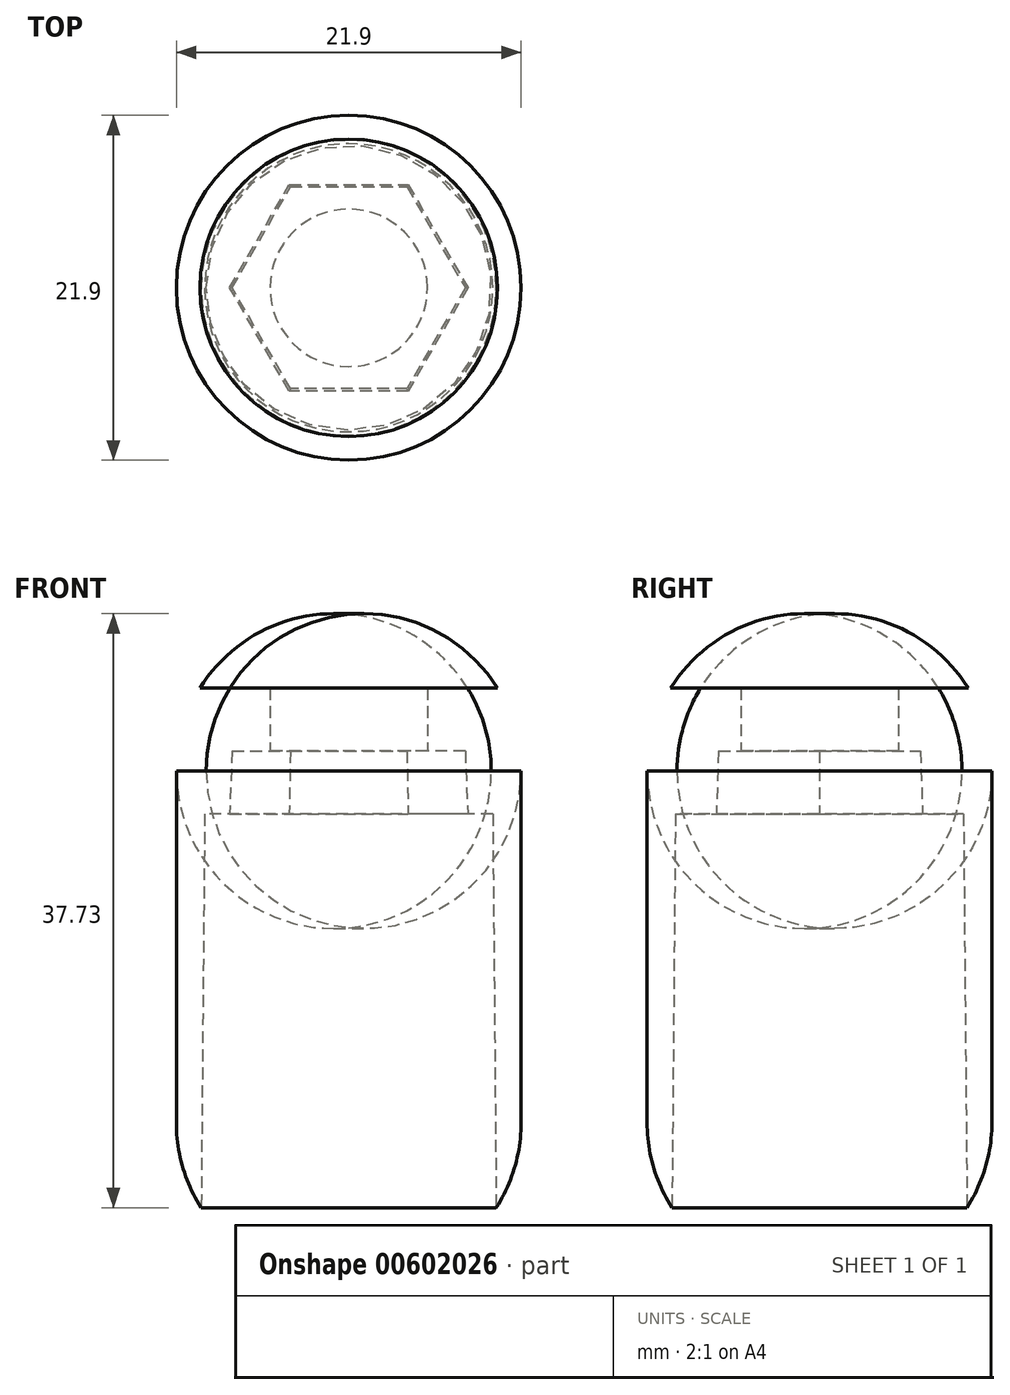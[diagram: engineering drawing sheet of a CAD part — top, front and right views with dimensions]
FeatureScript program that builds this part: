
annotation { "Feature Type Name" : "Feature", "Feature Type Description" : "" }
export const myFeature = defineFeature(function(context is Context, id is Id, definition is map)
    precondition{}
    {
        {
            var Q0;
            Q0=qCreatedBy(makeId("Top.planeOp"),FACE);
            var sketch = newSketch(context, id + "F0", { "sketchPlane" : qUnion([Q0])});
            skCircle(sketch, "E0", {"center": v(0, 0) * mm, "radius": 9.15 * mm});
            skCircle(sketch, "E1.cCircle", {"center": v(0, 0) * mm, "radius": 6.55 * mm, "construction": true});
            skLineSegment(sketch, "E1.0", {"start": v(-3.78, 6.55) * mm, "end": v(3.78, 6.55) * mm});
            skLineSegment(sketch, "E1.1", {"start": v(3.78, 6.55) * mm, "end": v(7.56, 0) * mm});
            skLineSegment(sketch, "E1.2", {"start": v(7.56, 0) * mm, "end": v(3.78, -6.55) * mm});
            skLineSegment(sketch, "E1.3", {"start": v(3.78, -6.55) * mm, "end": v(-3.78, -6.55) * mm});
            skLineSegment(sketch, "E1.4", {"start": v(-3.78, -6.55) * mm, "end": v(-7.56, 0) * mm});
            skLineSegment(sketch, "E1.5", {"start": v(-7.56, 0) * mm, "end": v(-3.78, 6.55) * mm});
            skPoint(sketch, "E1.0.midPoint", {"position": v(0, 6.55) * mm});
            skCircle(sketch, "E2.0", {"center": v(0, 0) * mm, "radius": 10.95 * mm});
            skSolve(sketch);
        }
        {
            var Q0;
            Q0=makeQuery(id+"F0.imprint","IMPRINT",FACE,{"disambiguationData":[TD([[makeQuery(id+"F0.imprint","IMPRINT",EDGE,{"derivedFrom":sQuery(id+"F0.wireOp",EDGE,"E0")}),-1.0]])]});
            extrude(context, id + "F1", {"entities" : qUnion([Q0]), "oppositeDirection" : true, "depth" : 25 * mm, "offsetDistance" : 25 * mm});
        }
        {
            var Q0;
            Q0=makeQuery(id+"F0.imprint","IMPRINT",FACE,{"disambiguationData":[TD([[makeQuery(id+"F0.imprint","IMPRINT",EDGE,{"derivedFrom":sQuery(id+"F0.wireOp",EDGE,"E0")}),1.0]])]});
            var Q1;
            Q1=makeQuery(id+"F0.imprint","IMPRINT",FACE,{"disambiguationData":[TD([[makeQuery(id+"F0.imprint","IMPRINT",EDGE,{"derivedFrom":sQuery(id+"F0.wireOp",EDGE,"E1.0")}),-1.0]])]});
            extrude(context, id + "F2", {"entities" : qUnion([Q0, Q1]), "operationType" : NewBodyOperationType.REMOVE, "oppositeDirection" : true, "depth" : 25 * mm, "offsetDistance" : 25 * mm, "hasDraft" : true, "draftAngle" : 0.5 * degree});
        }
        {
            var Q0;
            Q0=makeQuery(id+"F0.imprint","IMPRINT",FACE,{"disambiguationData":[TD([[makeQuery(id+"F0.imprint","IMPRINT",EDGE,{"derivedFrom":sQuery(id+"F0.wireOp",EDGE,"E1.0")}),-1.0]])]});
            var Q1;
            Q1=makeQuery(id+"F0.imprint","IMPRINT",FACE,{"disambiguationData":[TD([[makeQuery(id+"F0.imprint","IMPRINT",EDGE,{"derivedFrom":sQuery(id+"F0.wireOp",EDGE,"E0")}),1.0]])]});
            var Q2;
            Q2=makeQuery(id+"F0.imprint","IMPRINT",FACE,{"disambiguationData":[TD([[makeQuery(id+"F0.imprint","IMPRINT",EDGE,{"derivedFrom":sQuery(id+"F0.wireOp",EDGE,"E0")}),-1.0]])]});
            var Q3;
            Q3=sQuery(id+"F0.wireOp",EDGE,"E0");
            var Q4;
            Q4=sQuery(id+"F0.wireOp",EDGE,"E2.0");
            extrude(context, id + "F3", {"entities" : qUnion([Q0, Q1, Q2]), "operationType" : NewBodyOperationType.ADD, "surfaceEntities" : qUnion([Q3, Q4]), "depth" : 8 * mm, "offsetDistance" : 25 * mm});
        }
        {
            var Q0;
            Q0=makeQuery(id+"F0.imprint","IMPRINT",FACE,{"disambiguationData":[TD([[makeQuery(id+"F0.imprint","IMPRINT",EDGE,{"derivedFrom":sQuery(id+"F0.wireOp",EDGE,"E1.0")}),-1.0]])]});
            extrude(context, id + "F4", {"entities" : qUnion([Q0]), "operationType" : NewBodyOperationType.REMOVE, "depth" : 4 * mm, "offsetDistance" : 25 * mm, "hasDraft" : true, "draftAngle" : 2 * degree, "draftPullDirection" : true});
        }
        {
            var Q0;
            Q0=sQuery(id+"F0.wireOp",VERTEX,"E2.0.center");
            var Q1;
            Q1=makeQuery(id+"F1.opExtrude","SWEPT_BODY",BODY,{"disambiguationData":[OSD([sQuery(id+"F0.wireOp",EDGE,"E0"),sQuery(id+"F0.wireOp",EDGE,"E2.0")])]});
            hole(context, id + "F5", {"style" : HoleStyle.SIMPLE, "endStyle" : HoleEndStyle.BLIND, "oppositeDirection" : true, "holeDiameter" : 10 * mm, "majorDiameter" : 5 * mm, "holeDepth" : 15 * mm, "isTappedThrough" : true, "tappedDepth" : 12 * mm, "tapClearance" : 3, "locations" : qUnion([Q0]), "scope" : qUnion([Q1])});
        }
        {
            var Q0;
            {var subQ0=sQuery(id+"F0.wireOp",EDGE,"E0");Q0=makeQuery(id+"F2.boolean.opBoolean","MERGE",EDGE,{"derivedFrom":[makeQuery(id+"F1.opExtrude","CAP_EDGE",EDGE,{"disambiguationData":[OSD([subQ0])],"isStart":true}),makeQuery(id+"F2.opExtrude","CAP_EDGE",EDGE,{"disambiguationData":[OSD([subQ0])],"isStart":true})]});}
            var Q1;
            Q1=makeQuery(id+"F3.opExtrude","CAP_EDGE",EDGE,{"disambiguationData":[OSD([sQuery(id+"F0.wireOp",EDGE,"E2.0")])],"isStart":false});
            chamfer(context, id + "F6", {"entities" : qUnion([Q0, Q1]), "width" : 1.5 * mm, "tangentPropagation" : true});
        }
        {
            var Q0;
            Q0=makeQuery(id+"F1.opExtrude","CAP_EDGE",EDGE,{"disambiguationData":[OSD([sQuery(id+"F0.wireOp",EDGE,"E2.0")])],"isStart":false});
            var Q1;
            {var subQ0=sQuery(id+"F0.wireOp",EDGE,"E2.0");Q1=makeQuery(id+"F6.opChamfer","BLEND_EDGE",EDGE,{"blendedFrom":[makeQuery(id+"F3.opExtrude","CAP_EDGE",EDGE,{"disambiguationData":[OSD([subQ0])],"isStart":false}),makeQuery(id+"F3.boolean.opBoolean","MERGE",FACE,{"derivedFrom":[makeQuery(id+"F1.opExtrude","SWEPT_FACE",FACE,{"disambiguationData":[OSD([subQ0])]}),makeQuery(id+"F3.opExtrude","SWEPT_FACE",FACE,{"disambiguationData":[OSD([subQ0])]})]})],"blendedInto":[makeQuery(id+"F3.boolean.opBoolean","MERGE",FACE,{"derivedFrom":[makeQuery(id+"F1.opExtrude","SWEPT_FACE",FACE,{"disambiguationData":[OSD([subQ0])]}),makeQuery(id+"F3.opExtrude","SWEPT_FACE",FACE,{"disambiguationData":[OSD([subQ0])]})]})]});}
            fillet(context, id + "F7", {"entities" : qUnion([Q0, Q1]), "radius" : 10 * mm, "tangentPropagation" : true, "allowEdgeOverflow" : false});
        }
    });
